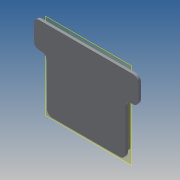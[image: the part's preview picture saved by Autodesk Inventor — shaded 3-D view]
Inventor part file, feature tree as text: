
AUTODESK INVENTOR PART (.ipt)
format: ipt  version: 2013 (Build 170138000, 138)  size: 215,040 bytes
history: native  units: in
note: dims shown in document units (in); Inventor stores cm internally (conversion verified against a paired STEP export)
features: extrude x6, sketch x6, reference x3, plane x1, mirror x1
ambient origin geometry x8: Origin, YZ Plane, XZ Plane, XY Plane, X Axis, Y Axis, Z Axis, Center Point
bodies: Solid1 (feature_tree)
feature tree (17):
  plane  "Work Plane1"
  extrude  "Extrusion1"  Depth=0.3937in TaperAngle=0.0deg
  extrude  "Extrusion2"  Depth=1.9685in
  extrude  "Extrusion3"  Depth=0.0197in
  extrude  "Extrusion4"  Depth=0.1969in TaperAngle=0.0deg
  extrude  "Extrusion5"  Depth=0.1181in TaperAngle=0.0deg
  mirror  "Mirror1"
  extrude  "Extrusion6"  Depth=0.1969in TaperAngle=0.0deg
  sketch  "Sketch1"  dims[d0=0.1969in d1=0.3937in d2=0.0in]
  reference  "Reference1"
  sketch  "Sketch2"  dims[d3=0.9843in d4=1.9685in]
  reference  "Reference2"
  sketch  "Sketch3"  dims[d5=0.1969in d6=0.0in d7=0.0197in]
  sketch  "Sketch4"  dims[d8=0.1969in d9=0.0in d10=0.1969in d11=0.0in]
  reference  "Reference3"
  sketch  "Sketch5"  dims[d12=0.2165in d13=0.1181in d14=0.0in]
  sketch  "Sketch6"  dims[d15=0.5906in d16=0.1969in d17=0.0in]
